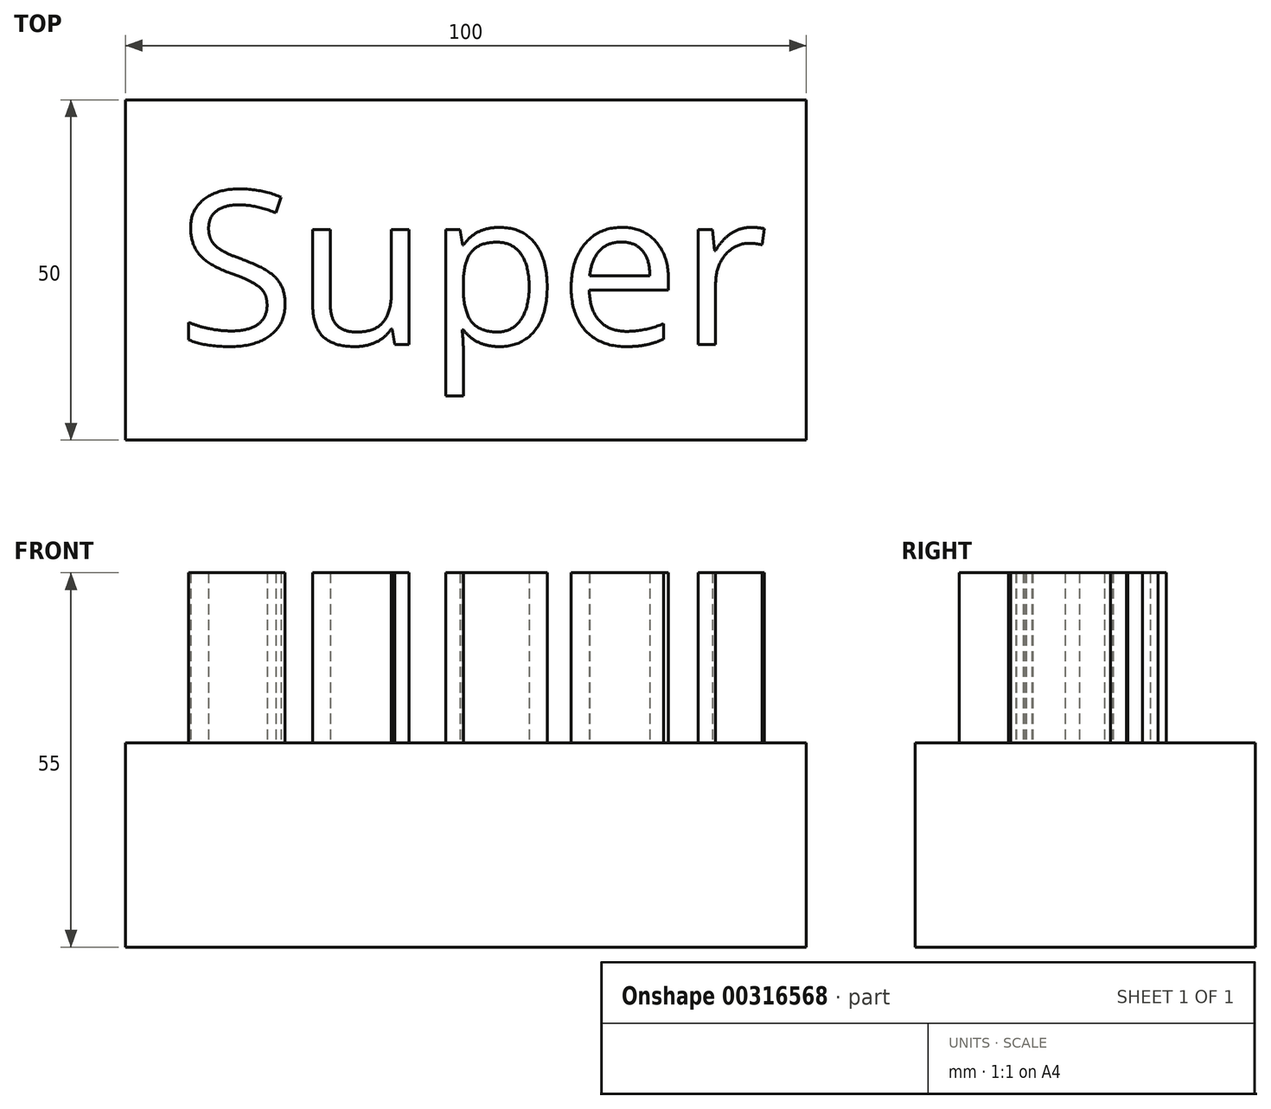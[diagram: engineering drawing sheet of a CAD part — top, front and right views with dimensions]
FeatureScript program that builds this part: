
annotation { "Feature Type Name" : "Feature", "Feature Type Description" : "" }
export const myFeature = defineFeature(function(context is Context, id is Id, definition is map)
    precondition{}
    {
        {
            var Q0;
            Q0=qCreatedBy(makeId("Top.planeOp"),FACE);
            var sketch = newSketch(context, id + "F0", { "sketchPlane" : qUnion([Q0])});
            skLineSegment(sketch, "E0.bottom", {"start": v(-50, 25) * mm, "end": v(50, 25) * mm});
            skLineSegment(sketch, "E0.top", {"start": v(-50, -25) * mm, "end": v(50, -25) * mm});
            skLineSegment(sketch, "E0.left", {"start": v(-50, 25) * mm, "end": v(-50, -25) * mm});
            skLineSegment(sketch, "E0.right", {"start": v(50, 25) * mm, "end": v(50, -25) * mm});
            skLineSegment(sketch, "E1", {"start": v(50, 25) * mm, "end": v(-50, -25) * mm, "construction": true});
            skSolve(sketch);
        }
        {
            var Q0;
            Q0 = qSketchRegion(id + "F0", true);
            extrude(context, id + "F1", {"entities" : qUnion([Q0]), "depth" : 30 * mm});
        }
        {
            var Q0;
            Q0=makeQuery(id+"F1.opExtrude","CAP_FACE",FACE,{"disambiguationData":[OSD([sQuery(id+"F0.wireOp",EDGE,"E0.bottom"),sQuery(id+"F0.wireOp",EDGE,"E0.top"),sQuery(id+"F0.wireOp",EDGE,"E0.left"),sQuery(id+"F0.wireOp",EDGE,"E0.right")])],"isStart":false});
            var sketch = newSketch(context, id + "F2", { "sketchPlane" : qUnion([Q0])});
            skText(sketch, "E2", { "text": "Super", "fontName": "OpenSans-Regular.ttf"});
            const initialGuessF2  = {"E2": [-0.04237, -0.01094, 1, 0, 0.02274]};
            skSetInitialGuess(sketch, initialGuessF2);
            skSolve(sketch);
        }
        {
            var Q0;
            Q0 = qSketchRegion(id + "F2", true);
            extrude(context, id + "F3", {"entities" : qUnion([Q0]), "operationType" : NewBodyOperationType.ADD, "depth" : 25 * mm});
        }
    });
